# Revit family: 005530
name_source: partatom
category: Generic Models
revit_build: Autodesk Revit 2018 (Build: 20170223_1515(x64)
units: mm (PartAtom-declared; Revit-internal decimal feet)

## family parameters
Can host rebar = No
Cut with Voids When Loaded = No
Host = Face
OmniClass Number = 23.80.70.00
OmniClass Title = Lighting
Part Type = Normal
Room Calculation Point = No
Round Connector Dimension = Use Diameter
Shared = No

## types (1)
- 0005531 LENZO SMALL 15W 930 ON BOARD DIM BLACK
    Adaptor length = 70 mm  [stored 0.229659 ft]
    Adaptor width = 32 mm  [stored 0.104987 ft]
    Assembly Code = D5020200
    Cost = 0 $
    Default Elevation = 1219 mm
    Description = The new generation of Lenzo improves the Sylvania track spot range with a simple and slick integral design fixture, with no driver box and no visible screws. Simple and integral design (diameter Ø60mm). Die cast aluminium body, passive cooling heat sink. Adjustable beam angle 15° - 50°. Textured Black - RAL 9005. Light color temperature: 3000K, warm white, total system power: 15W. Total fixture output: 1000lm, efficacy: 67lm/W, Ra90 typical, LED chromacity: 3 step MacAdam ellipse (SDCM3), IR/UV free light source without heat radiation, operating voltage: 220-240V / 50-60Hz. On Board dimming driver, ultra low flicker rate, power factor: >0.90, electrical protection: Class I. Degree of protection: IP20, suitable for indoor environment only. Suitable for 3-circuit tracks, horizontal rotation: 345°, vertical tilt: 90°. Dimensions: Ø60x229mm, weight: 0.48Kg.
    Height = 194 mm
    Length = 160 mm  [stored 0.524934 ft]
    Material_1_SYL = <By Category>
    Material_2_SYL = <By Category>
    Material_3_SYL = <By Category>
    Material_4_SYL = <By Category>
    Model = Lenzo Small 15W 930 On Board Dim Black
    Type Image = <None>
    URL = 0.9
    Width = 60 mm  [stored 0.19685 ft]

note: [stored X ft] marks values corroborated as IEEE doubles in the binary element streams (Revit-internal decimal feet)

## geometry (parser evidence)
native form markers: Sweep x33
no freeform markers — native parametric forms only
